# Revit family: MOMENTUM_ANGLED SHAPES_ TUXEDO
name_source: partatom
category: Generic Models
units: mm (PartAtom-declared; Revit-internal decimal feet)

## family parameters
Always vertical = Yes
Can host rebar = No
Cut with Voids When Loaded = No
Maintain Annotation Orientation = No
Part Type = Normal
Room Calculation Point = No
Round Connector Dimension = Use Diameter
Shared = No
Work Plane-Based = No

## types (19) — shared parameters
Assembly Code = C3010140
Description = DRESSED TO IMPRESS, with a 3D bowtie pattern in dynamic colors and texture patterns. Designed for mix and match play. Made from recycled PET felt (0.5"), Red List free with an NRC value of 0.45.
Installation Type = Construction Adhesive
Instruction Sheet Link = https://momentumtextilesandwalls-res.cloudinary.com
Keynote = 09840.A1
Manufacturer = Momentum
Material = 1/2" PET Felt
Product Documentation Link = https://momentumtextilesandwalls.com
URL = https://momentumtextilesandwalls.com
zero-valued in all types: Cost, Default Elevation

## per-type parameters (varying)
| type | Model | Pindrop Color | Product Name |
| Pindrop TUXEDO | 9579216 | <By Category> | PINDROP TUXEDO |
| clara_silk_tux-aegean-09574002 | 09574002 | Pindrop - Clara Silk Agean | PINDROP TUXEDO - Clara Silk |
| clara_silk_tux-cloudburst-09573958 | 09573958 | Pindrop - Clara Silk Cloudburst | PINDROP TUXEDO - Clara Silk |
| clara_silk_tux-mineral-09573969 | 09573969 | Pindrop - Clara Silk Mineral | PINDROP TUXEDO - Clara Silk |
| clara_silk_tux-nappa-09573980 | 09573980 | Pindrop - Clara Silk Nappa | PINDROP TUXEDO - Clara Silk |
| clara_silk_tux-stone-09573991 | 09573991 | Pindrop - Clara Silk Stone | PINDROP TUXEDO - Clara Silk |
| clara_silk_tux-terracotta-09574013 | 09574013 | Pindrop - Clara Silk Terracotta | PINDROP TUXEDO - Clara Silk |
| millinet_tux-andorra-09574035 | 09574035 | Pindrop - Millinet Andorra | PINDROP TUXEDO - Millinet |
| millinet_tux-brick-09574090 | 09574090 | Pindrop - Millinet Brick | PINDROP TUXEDO - Millinet |
| millinet_tux-cassite-09574046 | 09574046 | Pindrop - Millinet Cassite | PINDROP TUXEDO - Millinet |
| millinet_tux-earthen-09574068 | 09574068 | Pindrop - Millinet Earthen | PINDROP TUXEDO - Millinet |
| millinet_tux-oceanus-09574057 | 09574057 | Pindrop - Millinet Oceanus | PINDROP TUXEDO - Millinet |
| millinet_tux-pebble-09574079 | 09574079 | Pindrop - Millinet Pebble | PINDROP TUXEDO - Millinet |
| zuri_tux-ash-09574750 | 09574750 | Pindrop - Zuri Ash | PINDROP TUXEDO - Zuri |
| zuri_tux-bleached_oak-09574739 | 09574739 | Pindrop - Zuri Bleached Oak | PINDROP TUXEDO - Zuri |
| zuri_tux-ebony-09574783 | 09574783 | Pindrop - Zuri Ebony | PINDROP TUXEDO - Zuri |
| zuri_tux-mahogany-09574794 | 09574794 | Pindrop - Zuri Mahogany | PINDROP TUXEDO - Zuri |
| zuri_tux-walnut-09574761 | 09574761 | Pindrop - Zuri Walnut | PINDROP TUXEDO - Zuri |
| zuri_tux-weathered_oak-09574772 | 09574772 | Pindrop - Zuri Weathered Oak | PINDROP TUXEDO - Zuri |

## geometry (parser evidence)
native form markers: Sweep x7
no freeform markers — native parametric forms only
